# Revit family: Bath-Alcove-KOHLER-Bellwether-K-875
name_source: partatom
category: Plumbing Fixtures
revit_build: Autodesk Revit 2015 (Build: 20140606_1530(x64)
units: mm (PartAtom-declared; Revit-internal decimal feet)

## types (5) — shared parameters
ADA Compliant = Yes
Assembly Code = D2010500
CW Connection = No
Cold Water Inlet = Cold Water Inlet
Date Modified = 12/17/2018
Default Elevation = 0"
Description = 60inch x 32inch alcove bath with integral apron and left-hand drain
Drain Included = No
Environmental Product Declaration = https://www.us.kohler.com
HW Connection = No
Height = 15 1/2"
Hot Water Inlet = Hot Water Inlet
Length = 60"
Manufacturer = KOHLER Co.
MasterFormat 1995 = 15410
MasterFormat 2004 = 22.41.19
Material = Enameled Cast Iron
Product Documentation Link = http://www.us.kohler.com
Product Name = Bellwether
Product Page URL = http://www.us.kohler.com
URL = https://www.us.kohler.com
Vent Connection = No
Waste Connection = Yes
Waste Water Outlet = Waste Water Outlet
Width = 32"

## per-type parameters (varying)
| type | Finish | Model | Type |
| 0-White | Kohler-Enameled_Cast_Iron-0-White | K-875-0 | 1 |
| 96-Biscuit | Kohler-Enameled_Cast_Iron-96-Biscuit | K-875-96 | 2 |
| 47-Almond | Kohler-Enameled_Cast_Iron-47-Almond | K-875-47 | 3 |
| NY-Dune | Kohler-Enameled_Cast_Iron-NY-Dune | K-875-NY | 4 |
| G9-Sandbar | Kohler-Enameled_Cast_Iron-G9-Sandbar | K-875-G9 | 5 |

## geometry (parser evidence)
native form markers: Sweep x4
no freeform markers — native parametric forms only
